# Revit family: QF_BPRO_BC GF 8400_574205
name_source: partatom
category: Sonderausstattung
revit_build: Autodesk Revit 2018 (Build: 20190510_1515(x64)
units: mm (PartAtom-declared; Revit-internal decimal feet)

## family parameters
Arbeitsebenenbasiert = Nein
Beim Laden mit Abzugskörper schneiden = Nein
Bemaßung runder Anschluss = Durchmesser verwenden
Gemeinsam genutzt = Nein
Immer vertikal = Ja
Raumberechnungspunkt = Ja
Teiletyp = Normal

## types (1)
- BC GF 8400
    Artikel Nummer = 574205
    Becken Länge = 704 mm
    Becken Tiefe = 506 mm
    Becken Versatz von vorne = 58 mm
    Beckentiefe = 40 mm  [stored 0.131234 ft]
    Beschreibung = Grillplatte mit 2 getrennten Heizzonen
    Beschreibung durch Hersteller analog Leistungsverzeichniskurztext = BC GF 8400
Grillplatte, glatt
inkl. Fettablauf-Stopfen,
extrem leistungsstark
von +80 bis +250 °C,
2 getrennt regelbare
Heizzonen
    Beschreibung durch Hersteller analog Leistungsverzeichnislangtext = BC GF 8400
Grillplatte, glatt
inkl. Fettablauf-Stopfen,
extrem leistungsstark
von +80 bis +250 °C,
2 getrennt regelbare
Heizzonen
    CE Kennzeichnung = Ja
    Elektrische leistung = 8400 W
    Frequenz = 50 Hz
    Gerätegewicht Netto = 68.80 kg
    Großküchengerätezuordnung = Ja
    Hauptschalter integriert = Ja
    Hersteller = B.PRO GmbH
    Höhe = 240 mm
    Internetadresse Gerätehersteller = https://www.bpro-solutions.com
    Internetadresse für Ersatzteilliste = https://www.bpro-solutions.com
    Kosten = 5342 $
    Länge Gerätebreite = 800 mm
    Material = QF_Metal-Stainless-Steel_general
    Modell = BC GF 8400
    Phasen = 3
    Spannung = 400 V
    Tiefe = 620 mm
    Typenkommentare = Grillplatte BC GF 8400
    URL = https://www.bpro-solutions.com
    Zubehör = Ja
    Zuleitung zum Gerät im Lieferumfang = Ja

note: [stored X ft] marks values corroborated as IEEE doubles in the binary element streams (Revit-internal decimal feet)
